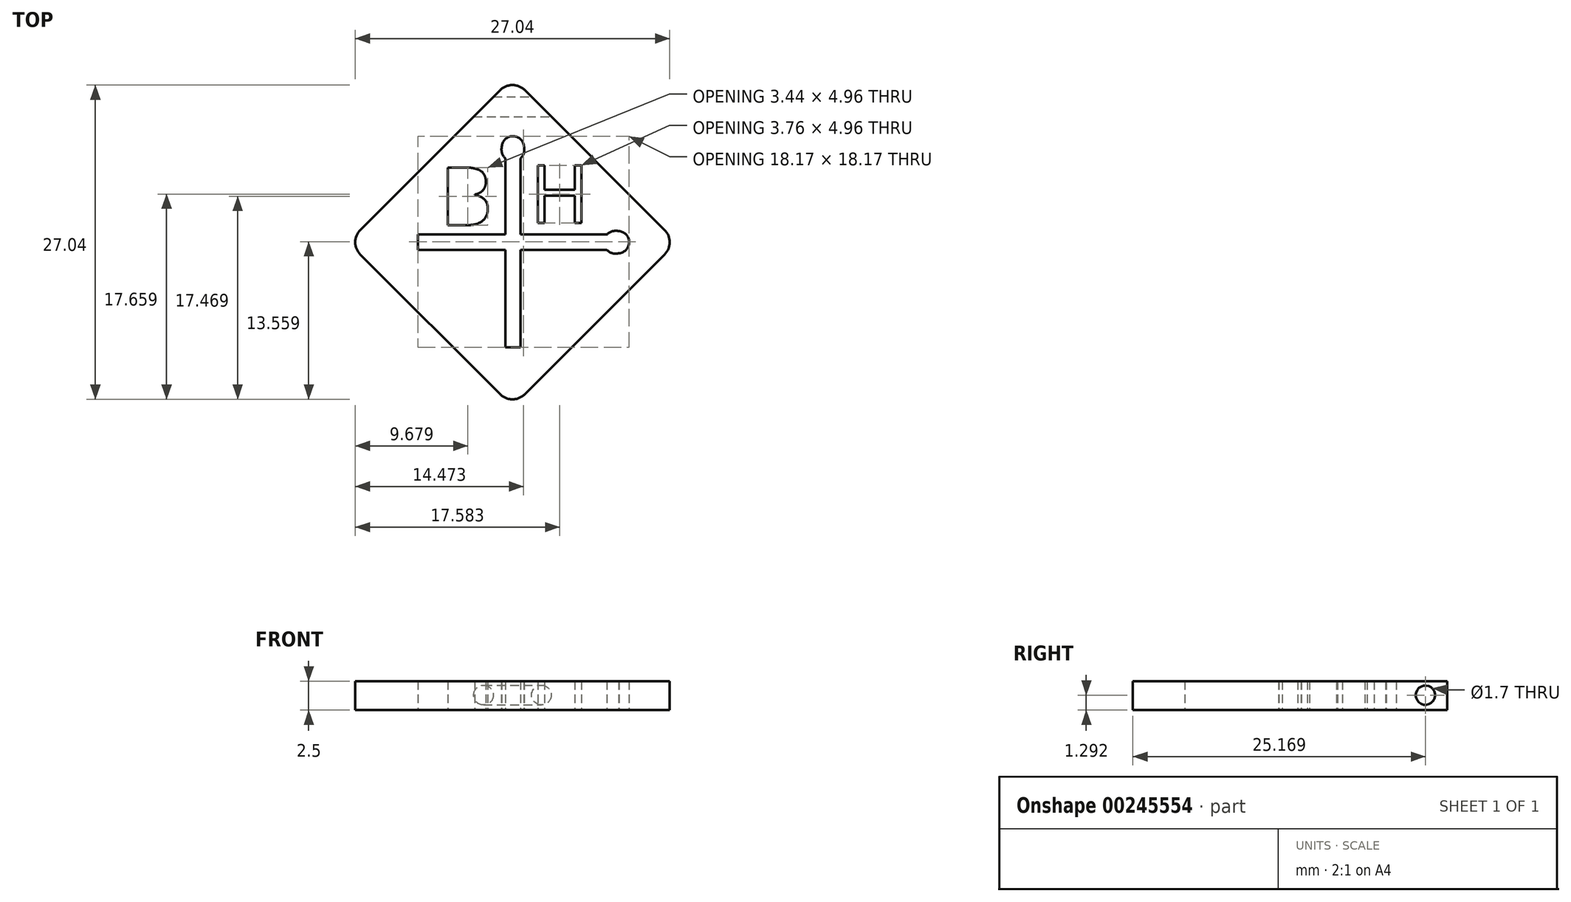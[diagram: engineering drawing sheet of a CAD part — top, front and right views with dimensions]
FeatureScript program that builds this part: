
annotation { "Feature Type Name" : "Feature", "Feature Type Description" : "" }
export const myFeature = defineFeature(function(context is Context, id is Id, definition is map)
    precondition{}
    {
        {
            var Q0;
            Q0=qCreatedBy(makeId("Top.planeOp"),FACE);
            var sketch = newSketch(context, id + "F0", { "sketchPlane" : qUnion([Q0])});
            skLineSegment(sketch, "E0", {"start": v(1.06, -1.06) * mm, "end": v(13.08, -13.08) * mm});
            skLineSegment(sketch, "E1", {"start": v(13.08, -15.2) * mm, "end": v(1.06, -27.22) * mm});
            skLineSegment(sketch, "E2", {"start": v(-1.06, -27.22) * mm, "end": v(-13.08, -15.2) * mm});
            skLineSegment(sketch, "E3", {"start": v(-13.08, -13.08) * mm, "end": v(-1.06, -1.06) * mm});
            skPoint(sketch, "E4.visualSharp", {"position": v(0, 0) * mm});
            skArc(sketch, "E4.filletArc", {"start": v(1.06, -1.06) * mm, "mid": v(0, -0.62) * mm, "end": v(-1.06, -1.06) * mm});
            skPoint(sketch, "E5.visualSharp", {"position": v(-14.14, -14.14) * mm});
            skArc(sketch, "E5.filletArc", {"start": v(-13.08, -13.08) * mm, "mid": v(-13.52, -14.14) * mm, "end": v(-13.08, -15.2) * mm});
            skPoint(sketch, "E6.visualSharp", {"position": v(14.14, -14.14) * mm});
            skArc(sketch, "E6.filletArc", {"start": v(13.08, -15.2) * mm, "mid": v(13.52, -14.14) * mm, "end": v(13.08, -13.08) * mm});
            skPoint(sketch, "E7.visualSharp", {"position": v(0, -28.28) * mm});
            skArc(sketch, "E7.filletArc", {"start": v(-1.06, -27.22) * mm, "mid": v(0, -27.66) * mm, "end": v(1.06, -27.22) * mm});
            skLineSegment(sketch, "E8", {"start": v(0, 0) * mm, "end": v(0, -31.86) * mm, "construction": true});
            skLineSegment(sketch, "E9", {"start": v(-14.14, -14.14) * mm, "end": v(14.14, -14.14) * mm, "construction": true});
            skLineSegment(sketch, "E10", {"start": v(-8.13, -13.48) * mm, "end": v(-8.13, -14.8) * mm});
            skLineSegment(sketch, "E11", {"start": v(-8.13, -14.8) * mm, "end": v(8.13, -14.8) * mm});
            skLineSegment(sketch, "E12", {"start": v(8.13, -13.48) * mm, "end": v(-8.13, -13.48) * mm});
            skLineSegment(sketch, "E13", {"start": v(-8.13, -13.48) * mm, "end": v(0, -13.48) * mm, "construction": true});
            skLineSegment(sketch, "E14", {"start": v(0, -13.48) * mm, "end": v(8.13, -13.48) * mm, "construction": true});
            skArc(sketch, "E15", {"start": v(9.18, -15.1) * mm, "mid": v(10.04, -14.12) * mm, "end": v(9.13, -13.2) * mm});
            skArc(sketch, "E16", {"start": v(9.13, -13.2) * mm, "mid": v(8.6, -13.2) * mm, "end": v(8.13, -13.48) * mm});
            skArc(sketch, "E17", {"start": v(8.13, -14.8) * mm, "mid": v(8.61, -15.1) * mm, "end": v(9.18, -15.1) * mm});
            skLineSegment(sketch, "E18", {"start": v(-0.62, -23.19) * mm, "end": v(0.7, -23.19) * mm});
            skLineSegment(sketch, "E19", {"start": v(0.7, -23.19) * mm, "end": v(0.7, -6.92) * mm});
            skLineSegment(sketch, "E20", {"start": v(-0.62, -6.92) * mm, "end": v(-0.62, -23.19) * mm});
            skLineSegment(sketch, "E21", {"start": v(-0.62, -23.19) * mm, "end": v(-0.62, -15.05) * mm, "construction": true});
            skLineSegment(sketch, "E22", {"start": v(-0.62, -15.05) * mm, "end": v(-0.62, -6.92) * mm, "construction": true});
            skArc(sketch, "E23", {"start": v(0.99, -5.88) * mm, "mid": v(0.02, -5.01) * mm, "end": v(-0.91, -5.92) * mm});
            skArc(sketch, "E24", {"start": v(-0.91, -5.92) * mm, "mid": v(-0.9, -6.46) * mm, "end": v(-0.62, -6.92) * mm});
            skArc(sketch, "E25", {"start": v(0.7, -6.92) * mm, "mid": v(1, -6.44) * mm, "end": v(0.99, -5.88) * mm});
            skText(sketch, "E26", { "text": "B", "fontName": "OpenSans-Regular.ttf"});
            skText(sketch, "E27", { "text": "H\n", "fontName": "OpenSans-Regular.ttf"});
            const initialGuessF0  = {"E26": [-0.00624, -0.01267, 1, 0, 0.005], "E27": [0.0015, -0.01248, 1, 0, 0.005]};
            skSetInitialGuess(sketch, initialGuessF0);
            skSolve(sketch);
        }
        {
            var Q0;
            Q0=makeQuery(id+"F0.imprint","IMPRINT",FACE,{"disambiguationData":[TD([[makeQuery(id+"F0.imprint","IMPRINT",EDGE,{"derivedFrom":sQuery(id+"F0.wireOp",EDGE,"E0")}),-1.0]])]});
            extrude(context, id + "F1", {"entities" : qUnion([Q0]), "depth" : 2.5 * mm});
        }
        {
            var Q0;
            Q0=qCreatedBy(makeId("Right.planeOp"),FACE);
            var sketch = newSketch(context, id + "F2", { "sketchPlane" : qUnion([Q0])});
            skCircle(sketch, "E28", {"center": v(-2.5, 1.3) * mm, "radius": 0.85 * mm});
            skSolve(sketch);
        }
        {
            var Q0;
            Q0=qSketchRegion(id+"F2",true);
            extrude(context, id + "F3", {"entities" : qUnion([Q0]), "operationType" : NewBodyOperationType.REMOVE, "endBound" : BoundingType.SYMMETRIC, "oppositeDirection" : true, "depth" : 25 * mm});
        }
    });
